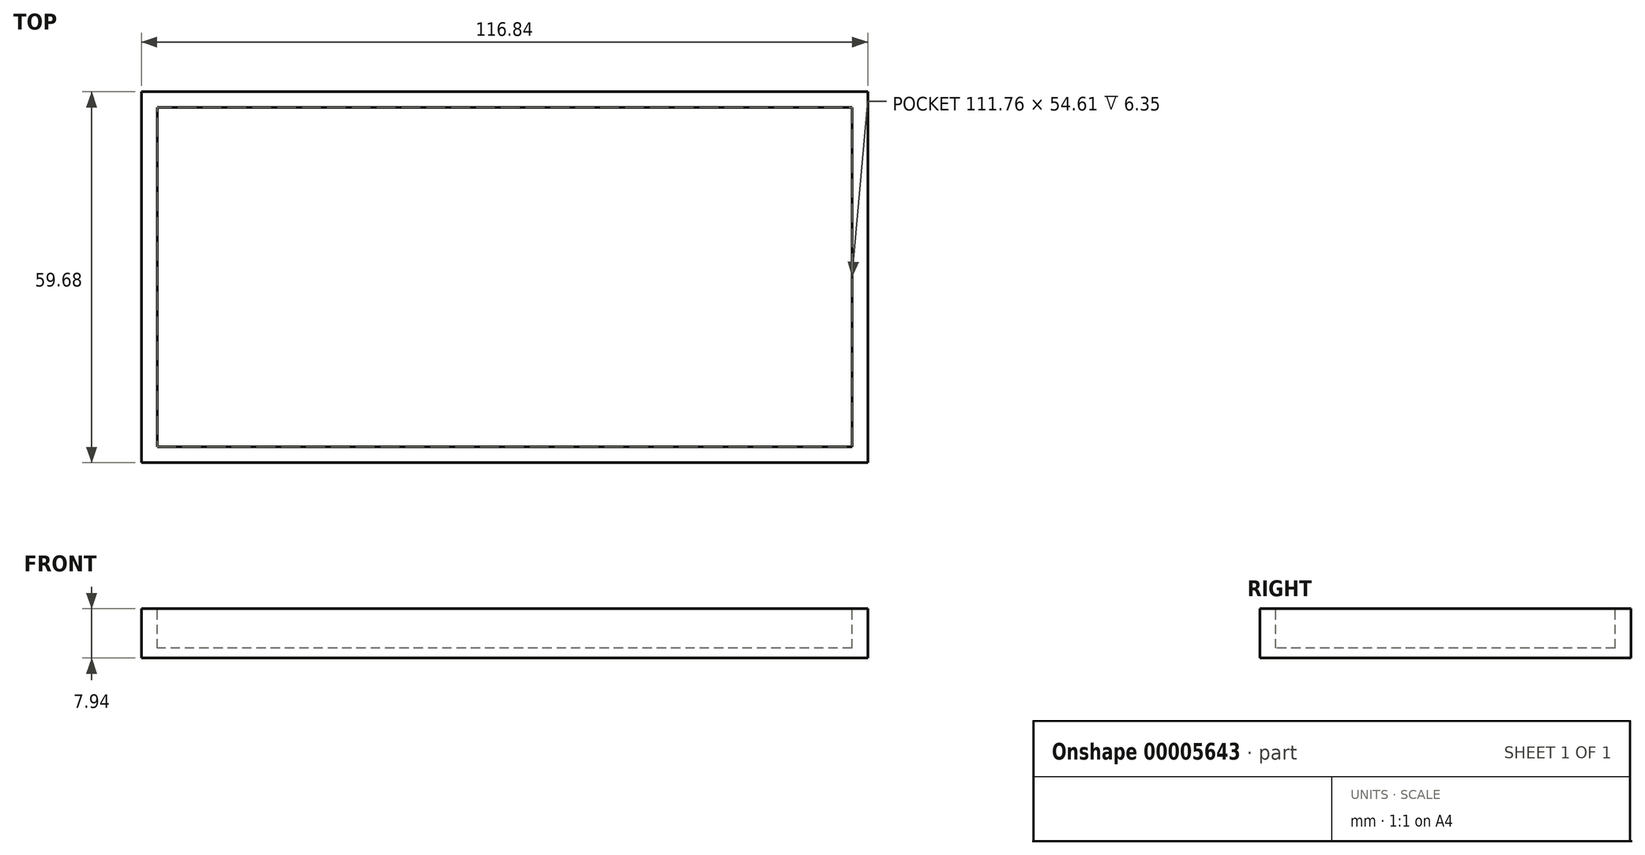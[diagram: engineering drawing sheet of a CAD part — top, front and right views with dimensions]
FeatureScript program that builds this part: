
annotation { "Feature Type Name" : "Feature", "Feature Type Description" : "" }
export const myFeature = defineFeature(function(context is Context, id is Id, definition is map)
    precondition{}
    {
        {
            var Q0;
            Q0=qCreatedBy(makeId("Top.planeOp"),FACE);
            var sketch = newSketch(context, id + "F0", { "sketchPlane" : qUnion([Q0])});
            skLineSegment(sketch, "E0.rect.bottom", {"start": v(58.42, 29.85) * mm, "end": v(-58.42, 29.84) * mm});
            skLineSegment(sketch, "E0.rect.top", {"start": v(58.42, -29.84) * mm, "end": v(-58.42, -29.85) * mm});
            skLineSegment(sketch, "E0.rect.left", {"start": v(58.42, 29.85) * mm, "end": v(58.42, -29.84) * mm});
            skLineSegment(sketch, "E0.rect.right", {"start": v(-58.42, 29.84) * mm, "end": v(-58.42, -29.85) * mm});
            skPoint(sketch, "E0.rect.middle", {"position": v(0, 0) * mm});
            skSolve(sketch);
        }
        {
            var Q0;
            Q0 = qSketchRegion(id + "F0", true);
            extrude(context, id + "F1", {"entities" : qUnion([Q0]), "depth" : 7.94 * mm});
        }
        {
            var Q0;
            Q0=makeQuery(id+"F1.opExtrude","CAP_FACE",FACE,{"disambiguationData":[OSD([sQuery(id+"F0.wireOp",EDGE,"E0.rect.bottom"),sQuery(id+"F0.wireOp",EDGE,"E0.rect.top"),sQuery(id+"F0.wireOp",EDGE,"E0.rect.left"),sQuery(id+"F0.wireOp",EDGE,"E0.rect.right")])],"isStart":false});
            var sketch = newSketch(context, id + "F2", { "sketchPlane" : qUnion([Q0])});
            skLineSegment(sketch, "E1.rect.bottom", {"start": v(55.88, 27.3) * mm, "end": v(-55.88, 27.3) * mm});
            skLineSegment(sketch, "E1.rect.top", {"start": v(55.88, -27.3) * mm, "end": v(-55.88, -27.3) * mm});
            skLineSegment(sketch, "E1.rect.left", {"start": v(55.88, 27.3) * mm, "end": v(55.88, -27.3) * mm});
            skLineSegment(sketch, "E1.rect.right", {"start": v(-55.88, 27.3) * mm, "end": v(-55.88, -27.3) * mm});
            skPoint(sketch, "E1.rect.middle", {"position": v(0, 0) * mm});
            skSolve(sketch);
        }
        {
            var Q0;
            Q0=makeQuery(id+"F2.imprint","IMPRINT",FACE,{"disambiguationData":[TD([[makeQuery(id+"F2.imprint","IMPRINT",EDGE,{"derivedFrom":sQuery(id+"F2.wireOp",EDGE,"E1.rect.bottom")}),1.0]])]});
            extrude(context, id + "F3", {"entities" : qUnion([Q0]), "operationType" : NewBodyOperationType.REMOVE, "oppositeDirection" : true, "depth" : 6.35 * mm});
        }
    });
